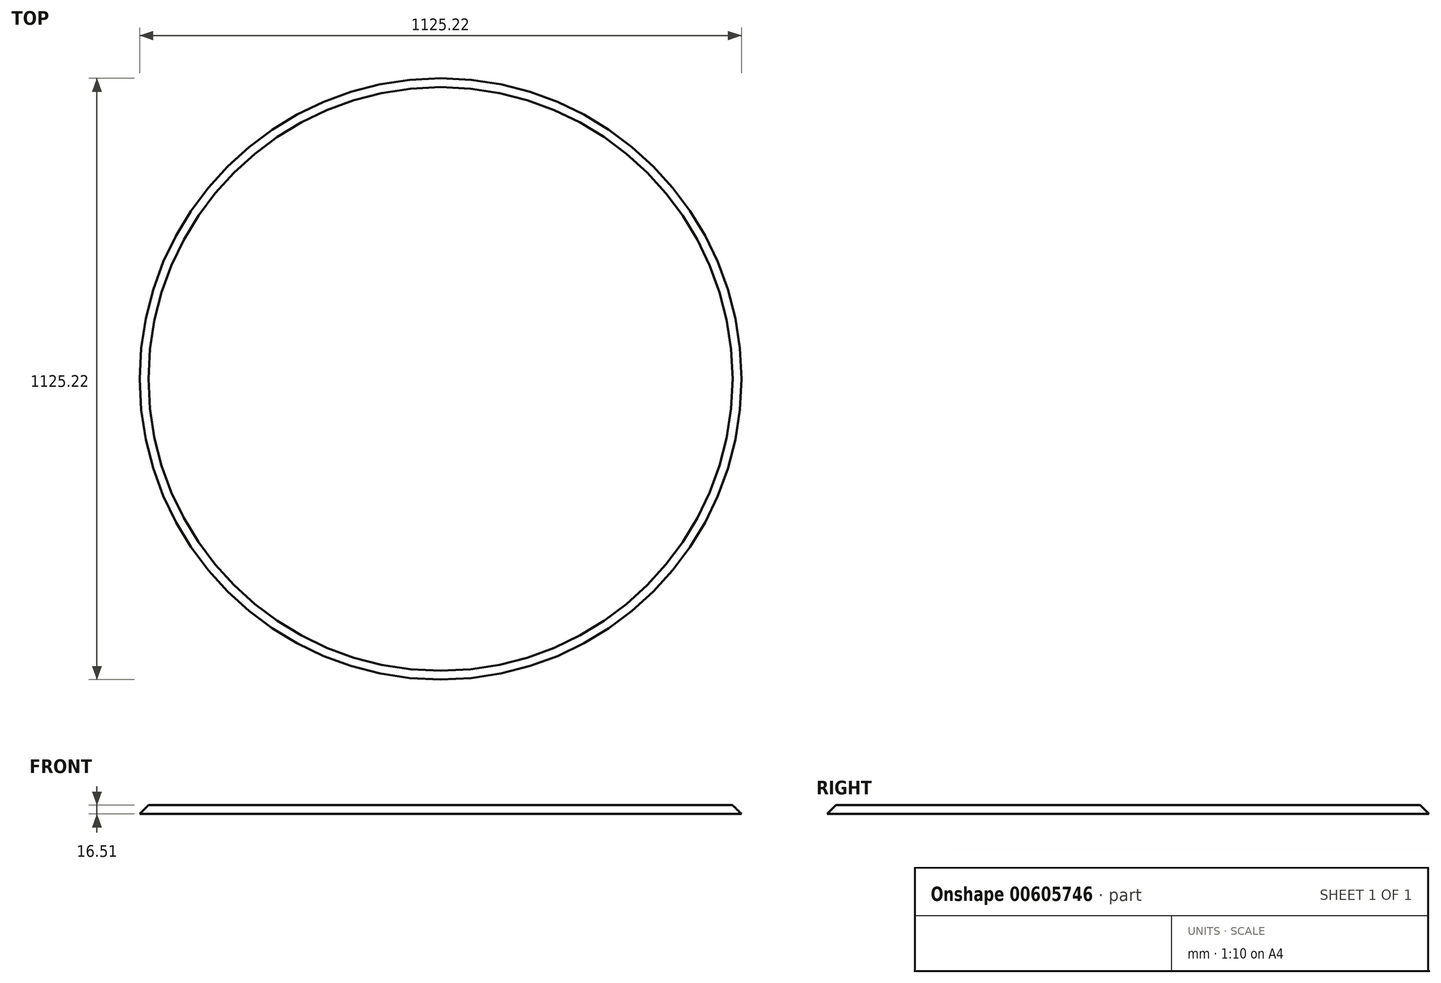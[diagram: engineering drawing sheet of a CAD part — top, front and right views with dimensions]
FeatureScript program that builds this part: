
annotation { "Feature Type Name" : "Feature", "Feature Type Description" : "" }
export const myFeature = defineFeature(function(context is Context, id is Id, definition is map)
    precondition{}
    {
        {
            var Q0;
            Q0=qCreatedBy(makeId("Top.planeOp"),FACE);
            var sketch = newSketch(context, id + "F0", { "sketchPlane" : qUnion([Q0])});
            skCircle(sketch, "E0", {"center": v(0, 0) * mm, "radius": 571.5 * mm});
            skSolve(sketch);
        }
        {
            var Q0;
            Q0 = qSketchRegion(id + "F0", true);
            extrude(context, id + "F1", {"entities" : qUnion([Q0]), "depth" : 12.7 * mm, "offsetDistance" : 25.4 * mm});
        }
        {
            var Q0;
            Q0=makeQuery(id+"F1.opExtrude","CAP_FACE",FACE,{"disambiguationData":[OSD([sQuery(id+"F0.wireOp",EDGE,"E0")])],"isStart":false});
            extrude(context, id + "F2", {"entities" : qUnion([Q0]), "operationType" : NewBodyOperationType.ADD, "depth" : 3.8 * mm, "offsetDistance" : 25.4 * mm});
        }
        {
            var Q0;
            Q0=makeQuery(id+"F2.opExtrude","CAP_EDGE",EDGE,{"disambiguationData":[OSD([sQuery(id+"F0.wireOp",EDGE,"E0")])],"isStart":false});
            chamfer(context, id + "F3", {"entities" : qUnion([Q0]), "width" : 25.4 * mm, "tangentPropagation" : true});
        }
    });
